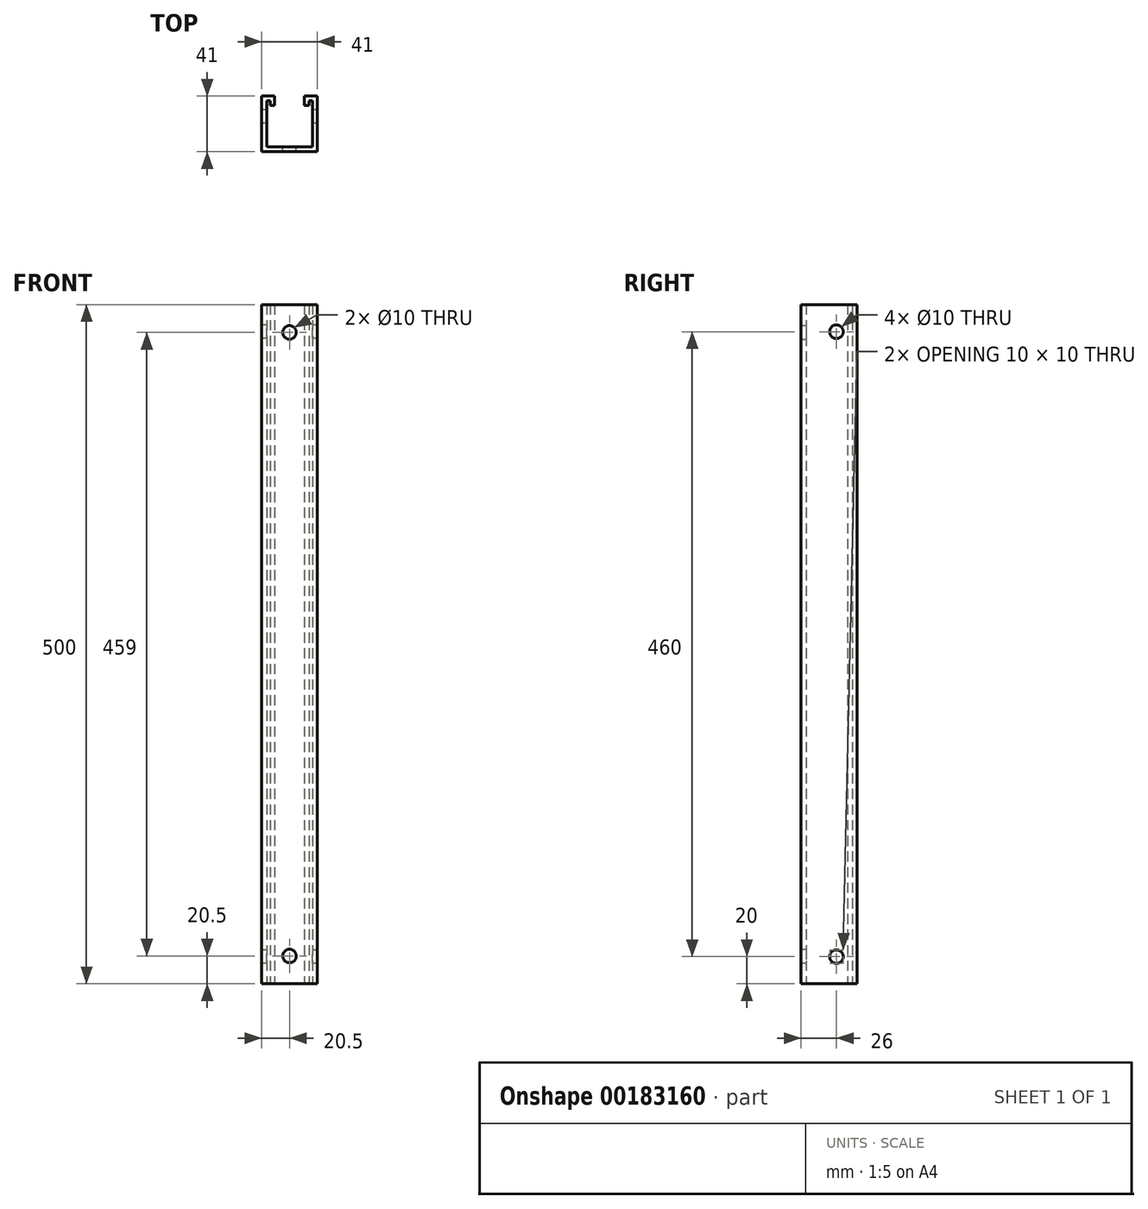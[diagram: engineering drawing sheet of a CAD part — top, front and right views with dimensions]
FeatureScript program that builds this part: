
annotation { "Feature Type Name" : "Feature", "Feature Type Description" : "" }
export const myFeature = defineFeature(function(context is Context, id is Id, definition is map)
    precondition{}
    {
        {
            var Q0;
            Q0=qCreatedBy(makeId("Top.planeOp"),FACE);
            var sketch = newSketch(context, id + "F0", { "sketchPlane" : qUnion([Q0])});
            skLineSegment(sketch, "E0", {"start": v(0, 0) * mm, "end": v(41, 0) * mm});
            skLineSegment(sketch, "E1", {"start": v(41, 0) * mm, "end": v(41, 41) * mm});
            skLineSegment(sketch, "E2", {"start": v(41, 41) * mm, "end": v(31.4, 41) * mm});
            skLineSegment(sketch, "E3", {"start": v(31.4, 41) * mm, "end": v(31.4, 34) * mm});
            skLineSegment(sketch, "E4", {"start": v(31.4, 34) * mm, "end": v(34.8, 34) * mm});
            skLineSegment(sketch, "E5", {"start": v(34.8, 34) * mm, "end": v(34.8, 37.5) * mm});
            skLineSegment(sketch, "E6", {"start": v(34.8, 37.5) * mm, "end": v(37.3, 37.5) * mm});
            skLineSegment(sketch, "E7", {"start": v(37.3, 37.5) * mm, "end": v(37.3, 3.7) * mm});
            skLineSegment(sketch, "E8", {"start": v(37.3, 3.7) * mm, "end": v(3.7, 3.7) * mm});
            skLineSegment(sketch, "E9", {"start": v(0, 0) * mm, "end": v(0, 41) * mm});
            skLineSegment(sketch, "E10", {"start": v(0, 41) * mm, "end": v(9.6, 41) * mm});
            skLineSegment(sketch, "E11", {"start": v(9.6, 41) * mm, "end": v(9.6, 34) * mm});
            skLineSegment(sketch, "E12", {"start": v(9.6, 34) * mm, "end": v(6.2, 34) * mm});
            skLineSegment(sketch, "E13", {"start": v(6.2, 34) * mm, "end": v(6.2, 37.5) * mm});
            skLineSegment(sketch, "E14", {"start": v(6.2, 37.5) * mm, "end": v(3.7, 37.5) * mm});
            skLineSegment(sketch, "E15", {"start": v(3.7, 37.5) * mm, "end": v(3.7, 3.7) * mm});
            skSolve(sketch);
        }
        {
            var Q0;
            Q0 = qSketchRegion(id + "F0", true);
            extrude(context, id + "F1", {"entities" : qUnion([Q0]), "depth" : 500 * mm});
        }
        {
            var Q0;
            Q0=makeQuery(id+"F1.opExtrude","SWEPT_FACE",FACE,{"disambiguationData":[OSD([sQuery(id+"F0.wireOp",EDGE,"E8")])]});
            var sketch = newSketch(context, id + "F2", { "sketchPlane" : qUnion([Q0])});
            skCircle(sketch, "E16", {"center": v(-20.5, 479.5) * mm, "radius": 5 * mm});
            skPoint(sketch, "E16.centerSnap0", {"position": v(-20.5, 500) * mm});
            skCircle(sketch, "E17", {"center": v(-20.5, 20.5) * mm, "radius": 5 * mm});
            skPoint(sketch, "E17.centerSnap0", {"position": v(-20.5, 0) * mm});
            skSolve(sketch);
        }
        {
            var Q0;
            Q0 = qSketchRegion(id + "F2", true);
            extrude(context, id + "F3", {"entities" : qUnion([Q0]), "operationType" : NewBodyOperationType.REMOVE, "endBound" : BoundingType.UP_TO_NEXT, "oppositeDirection" : true, "depth" : 25 * mm});
        }
        {
            var Q0;
            Q0=makeQuery(id+"F1.opExtrude","SWEPT_FACE",FACE,{"disambiguationData":[OSD([sQuery(id+"F0.wireOp",EDGE,"E9")])]});
            var sketch = newSketch(context, id + "F4", { "sketchPlane" : qUnion([Q0])});
            skCircle(sketch, "E18", {"center": v(-26, 20) * mm, "radius": 5 * mm});
            skCircle(sketch, "E19", {"center": v(-26, 480) * mm, "radius": 5 * mm});
            skSolve(sketch);
        }
        {
            var Q0;
            Q0 = qSketchRegion(id + "F4", true);
            extrude(context, id + "F5", {"entities" : qUnion([Q0]), "operationType" : NewBodyOperationType.REMOVE, "endBound" : BoundingType.THROUGH_ALL, "oppositeDirection" : true, "depth" : 25 * mm});
        }
    });
